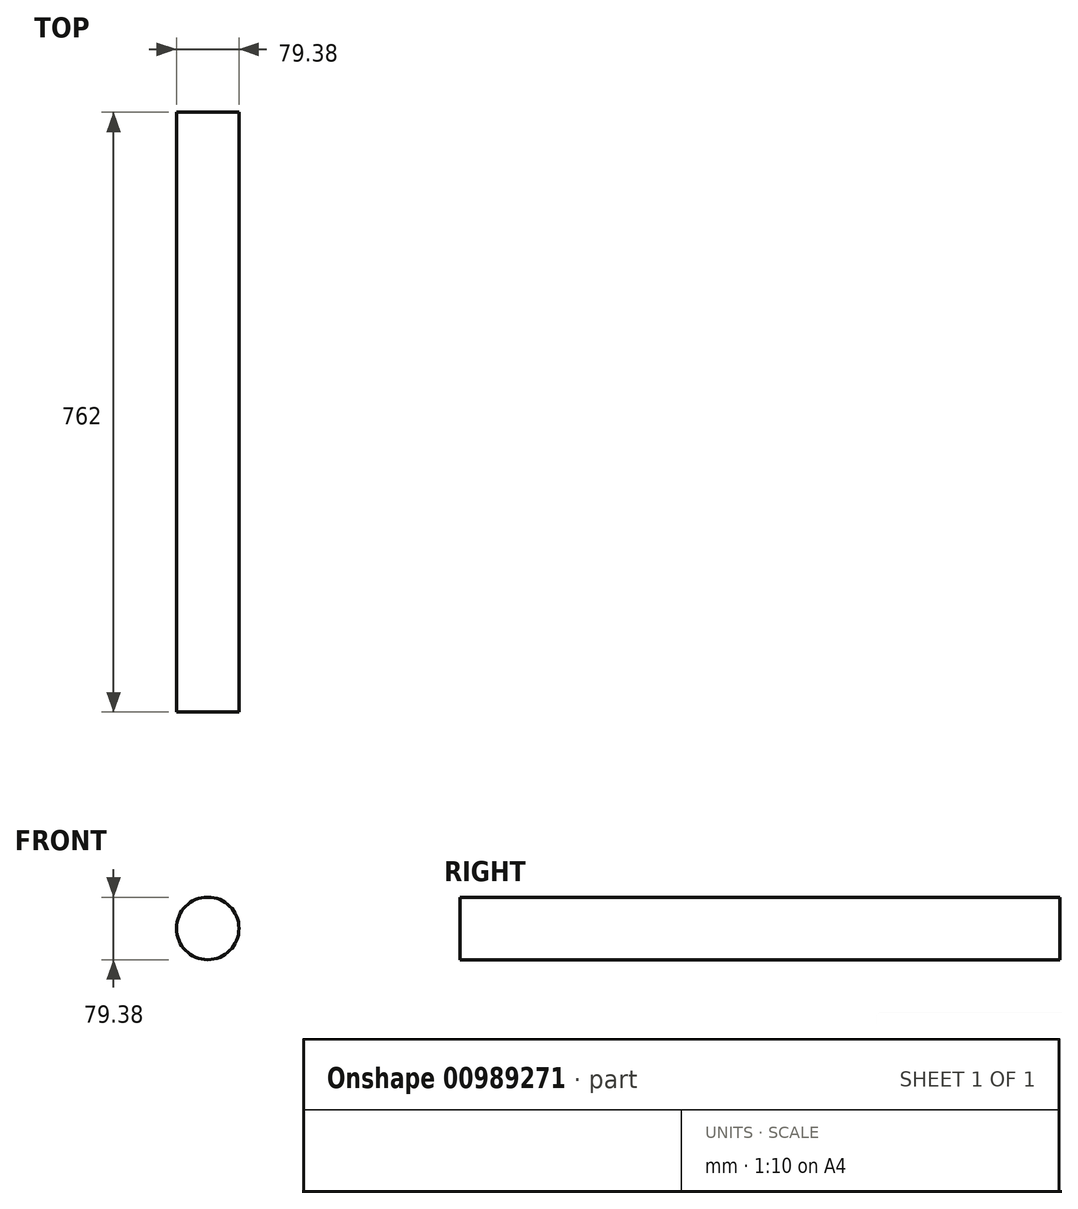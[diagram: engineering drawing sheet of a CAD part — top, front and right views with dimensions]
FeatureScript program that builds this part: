
annotation { "Feature Type Name" : "Feature", "Feature Type Description" : "" }
export const myFeature = defineFeature(function(context is Context, id is Id, definition is map)
    precondition{}
    {
        {
            var Q0;
            Q0=qCreatedBy(makeId("Front.planeOp"),FACE);
            var sketch = newSketch(context, id + "F0", { "sketchPlane" : qUnion([Q0])});
            skCircle(sketch, "E0", {"center": v(0, 0) * mm, "radius": 39.69 * mm});
            skSolve(sketch);
        }
        {
            var Q0;
            Q0=makeQuery(id+"F0.imprint","IMPRINT",FACE,{"disambiguationData":[TD([[makeQuery(id+"F0.imprint","IMPRINT",EDGE,{"derivedFrom":sQuery(id+"F0.wireOp",EDGE,"E0")}),1.0]])]});
            extrude(context, id + "F1", {"entities" : qUnion([Q0]), "depth" : 762 * mm, "offsetDistance" : 25.4 * mm});
        }
    });
